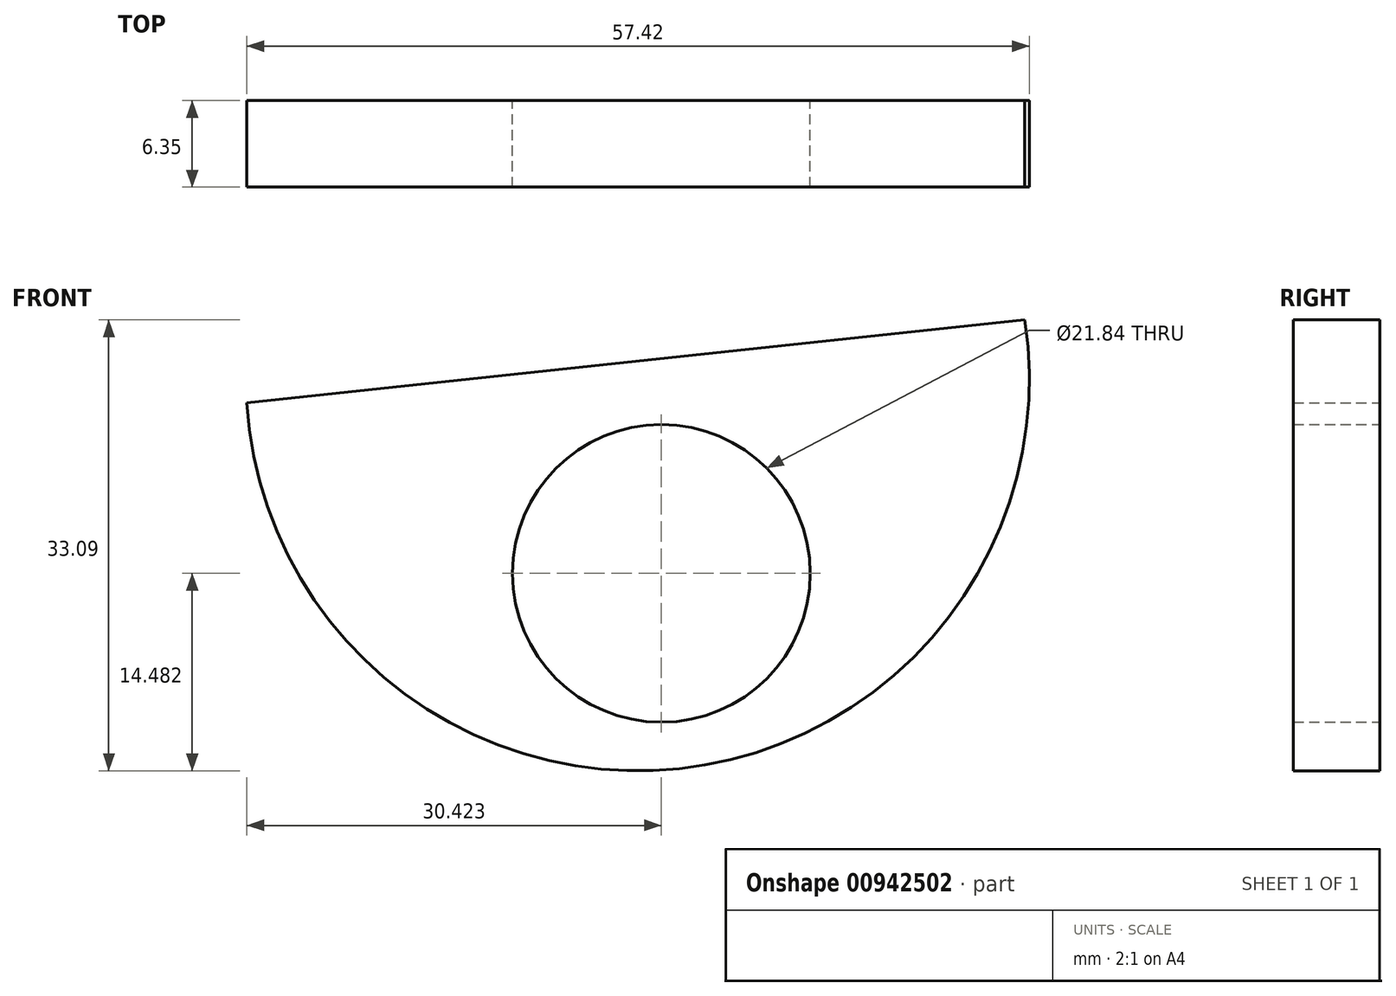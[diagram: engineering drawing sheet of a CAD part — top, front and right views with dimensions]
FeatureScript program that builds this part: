
annotation { "Feature Type Name" : "Feature", "Feature Type Description" : "" }
export const myFeature = defineFeature(function(context is Context, id is Id, definition is map)
    precondition{}
    {
        {
            var Q0;
            Q0=qCreatedBy(makeId("Front.planeOp"),FACE);
            var sketch = newSketch(context, id + "F0", { "sketchPlane" : qUnion([Q0])});
            skArc(sketch, "E0", {"start": v(-62.47, 44.74) * mm, "mid": v(-30.74, 17.89) * mm, "end": v(-5.38, 50.82) * mm});
            skLineSegment(sketch, "E1", {"start": v(-62.47, 44.74) * mm, "end": v(-5.38, 50.82) * mm});
            skCircle(sketch, "E2", {"center": v(-32.05, 32.21) * mm, "radius": 10.92 * mm});
            skSolve(sketch);
        }
        {
            var Q0;
            Q0 = qSketchRegion(id + "F0", true);
            extrude(context, id + "F1", {"entities" : qUnion([Q0]), "depth" : 6.35 * mm, "offsetDistance" : 25.4 * mm});
        }
    });
